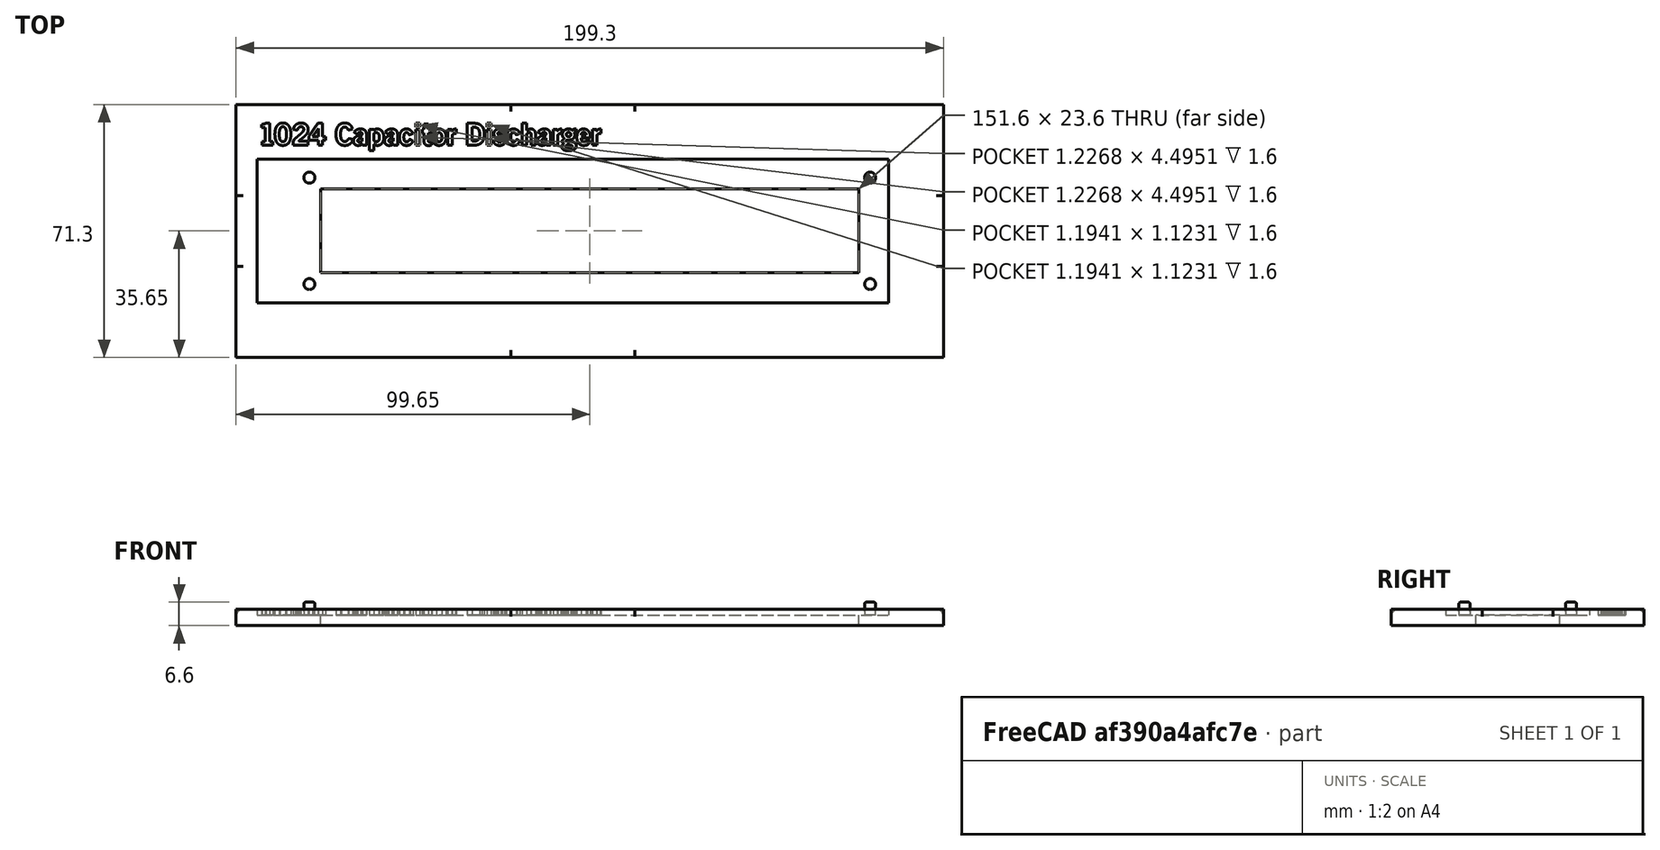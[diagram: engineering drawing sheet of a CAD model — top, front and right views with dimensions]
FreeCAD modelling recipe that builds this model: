
FCSTD DOCUMENT  (FreeCAD 0.21R33771 (Git))
Label: Solder Stencil Jig V2
License: All rights reserved
LicenseURL: http://en.wikipedia.org/wiki/All_rights_reserved
objects: Sketcher::SketchObject×6, PartDesign::Pocket×4, PartDesign::Pad×3, Spreadsheet::Sheet×1, Part::Part2DObjectPython×1, PartDesign::Fillet×1, PartDesign::Body×1, App::Part×1, Mesh::Feature×1
note: 24 computed .brp shape members not serialized (recipe doc carries the construction recipe); baked Part::Feature solids carry a one-line shape summary decoded from their .brp

FEATURE [Spreadsheet::Sheet] Spreadsheet  label="S"
  cells = A1='1024 Capacitor Discharger; A2='Solder Stencil Jig; A4='Board Edge Dimension X; B4='pcb_x; C4(pcb_x)==177.5 mm; D4='Design X dimension of PCB; A5='Board Edge Dimension Y; B5='pcb_y; C5(pcb_y)==40 mm; D5='Design Y dimension of PCB; A6='Board Thickness Z; B6='pcb_z; C6(pcb_z)==1.6 mm; D6='Design Z (thickness) dimension of PCB; A7='Mounting Hole 1 X Coordinate; B7='h1_x; C7(h1_x)==14.5 mm; D7='Relative to lower left corner of PCB, positive X to right, positive Y to top, note the Y coordinate sign is opposite KiCAD; A8='Mounting Hole 1 Y Coordinate; B8='h1_y; C8(h1_y)==5 mm; D8='Mounting Hole 1 = Lower Left, will be one of the registration pins; A9='Mounting Hole 1 Diameter; B9='h1_d; C9(h1_d)==3.2 mm; A10='Mounting Hole 2 X Coordinate; B10='h2_x; C10(h2_x)==14.5 mm; D10='Mounting Hole 2 = Upper Left, no registration; A11='Mounting Hole 2 Y Coordinate; B11='h2_y; C11(h2_y)==35 mm; A12='Mounting Hole 2 Diameter; B12='h2_d; C12(h2_d)==3.2 mm; A13='Mounting Hole 3 X Coordinate; B13='h3_x; C13(h3_x)==172.5 mm; D13='Mounting Hole 3 = Upper Right, will be one of the registration pins; A14='Mounting Hole 3 Y Coordinate; B14='h3_y; C14(h3_y)==35 mm; A15='Mounting Hole 3 Diameter; B15='h3_d; C15(h3_d)==3.2 mm; A16='Mounting Hole 4 X Coordinate; B16='h4_x; C16(h4_x)==172.5 mm; D16='Mounting Hole 4 = Lower Right, no registration; A17='Mounting Hole 4 Y Coordinate; B17='h4_y; C17(h4_y)==5 mm; A18='Mounting Hole 4 Diameter; B18='h4_d; C18(h4_d)==3.2 mm; A19='Holding Ledge Top; B19='hold_t; C19(hold_t)==8.2 mm; D19='The distance of the edge of the printed jig that will hold the PCB from the bottom, make sure this clears any bottom-mounted components; A20='Holding Ledge Bottom; B20='hold_b; C20(hold_b)==8.2 mm; D20='But, the ledges must encompass all mounting holes; A21='Holding Ledge Left; B21='hold_l; C21(hold_l)==17.7 mm; A22='Holding Ledge Right; B22='hold_r; C22(hold_r)==8.2 mm; A23='Bottom PCB Component Clearance; B23='hold_h; C23(hold_h)==3 mm; D23='The window underneath the PCB will be this far off the bottom surface to allow bottom-mounted components clearance; A24='Board-Jig Edge Clearance; B24='edge_clr; C24(edge_clr)==0.25 mm; D24='The window where the PCB sits will be backset from the board edge by this amount on each edge; A25='Mounting Hole Clearance; B25='mh_clr; C25(mh_clr)==0.1 mm; D25='The jig pins and registration pins that go through the mounting holes will clear the PCB by this amount; A26='Registration Pin Height; B26='reg_h; C26(reg_h)==2 mm; D26='The registration pins will be above the PCB surface by this amount to hold the stencil; A27='Jig Oversize Left; B27='jigovr_l; C27(jigovr_l)==6.15 mm; D27='The jig will be this much larger than the PCB in the X direction on the left side, make this at least as large as your stencil; A28='Jig Oversize Right; B28='jigovr_r; C28(jigovr_r)==15.65 mm; D28='The jig will be this much larger than the PCB in the X direction on the right side, make this at least as large as your stencil; A29='Jig Oversize Top; B29='jigove_t; C29(jigove_t)==15.65 mm; D29='The jig will be this much larger than the PCB in the Y direction on the top side, make this at least as large as your stencil; A30='Jig Oversize Bottom; B30='jigovr_b; C30(jigovr_b)==15.65 mm; D30='The jig will be this much larger than the PCB in the Y direction on the bottom side, make this at least as large as your stencil; A31='Jig Top Text; B31='text; C31(text)='1024 Capacitor Discharger; D31='This text will be embossed on the top of the jig; A32='Jig Edge Relief Round Diameter; B32='relf_r; C32(relf_r)==2 mm; D32='The reliefs on the edge of the jig will be rounded to this radius; A33='Jig Edge Relief Size T-B; B33='relf_stb; C33(relf_stb)==35 mm; D33='The reliefs on the top/bottom edge of the jig will be this long, centered on each edge; A34='Jig Edge Relief Size L-R; B34='relf_slr; C34(relf_slr)==20 mm; D34='The reliefs on the left/right edge of the jig will be this long, centered on each edge
FEATURE [Sketcher::SketchObject] Sketch  label="Sketch-Bottom"
  FullyConstrained = true
  MapMode = 5
  Support = -> [XY_Plane001]
  expr: Constraints[10] = <<S>>.pcb_y - <<S>>.hold_b - <<S>>.hold_t
  expr: Constraints[11] = <<S>>.pcb_x - <<S>>.hold_l - <<S>>.hold_r
  expr: Constraints[20] = <<S>>.jigovr_l
  expr: Constraints[21] = <<S>>.jigovr_b
  expr: Constraints[22] = <<S>>.pcb_x + <<S>>.jigovr_l + <<S>>.jigovr_r
  expr: Constraints[23] = <<S>>.pcb_y + <<S>>.jigovr_b + <<S>>.jigove_t
  expr: Constraints[8] = <<S>>.hold_l
  expr: Constraints[9] = <<S>>.hold_b
  sketch-geometry (8):
    g0: LineSegment StartX=17.7 StartY=8.2 StartZ=0 EndX=169.3 EndY=8.2 EndZ=0
    g1: LineSegment StartX=169.3 StartY=8.2 StartZ=0 EndX=169.3 EndY=31.8 EndZ=0
    g2: LineSegment StartX=169.3 StartY=31.8 StartZ=0 EndX=17.7 EndY=31.8 EndZ=0
    g3: LineSegment StartX=17.7 StartY=31.8 StartZ=0 EndX=17.7 EndY=8.2 EndZ=0
    g4: LineSegment StartX=-6.15 StartY=55.65 StartZ=0 EndX=193.15 EndY=55.65 EndZ=0
    g5: LineSegment StartX=193.15 StartY=55.65 StartZ=0 EndX=193.15 EndY=-15.65 EndZ=0
    g6: LineSegment StartX=193.15 StartY=-15.65 StartZ=0 EndX=-6.15 EndY=-15.65 EndZ=0
    g7: LineSegment StartX=-6.15 StartY=-15.65 StartZ=0 EndX=-6.15 EndY=55.65 EndZ=0
  constraints (24):
    c: Coincident(g0,g1)
    c: Coincident(g1,g2)
    c: Coincident(g2,g3)
    c: Coincident(g3,g0)
    c: Horizontal(g0)
    c: Horizontal(g2)
    c: Vertical(g1)
    c: Vertical(g3)
    c: DistanceX(g-1,g0) = 17.7
    c: DistanceY(g-1,g0) = 8.2
    c: DistanceY(g3,g3) = 23.6
    c: DistanceX(g2,g2) = 151.6
    c: Coincident(g4,g5)
    c: Coincident(g5,g6)
    c: Coincident(g6,g7)
    c: Coincident(g7,g4)
    c: Horizontal(g4)
    c: Horizontal(g6)
    c: Vertical(g5)
    c: Vertical(g7)
    c: DistanceX(g6,g-1) = 6.15
    c: DistanceY(g6,g-1) = 15.65
    c: DistanceX(g6,g6) = 199.3
    c: DistanceY(g7,g7) = 71.3
FEATURE [PartDesign::Pad] Pad  label="Pad-MainJig"
  Direction = (0,0,1)
  Length = 4.6
  Length2 = 10
  Profile = -> Sketch
  ReferenceAxis = -> Sketch [N_Axis]
  Type = 0
  expr: Length = <<S>>.pcb_z + <<S>>.hold_h
FEATURE [Sketcher::SketchObject] Sketch001  label="Sketch-PCB"
  AttachmentOffset = pos=(0,0,4.6) rot=(0,0,1;0rad)
  FullyConstrained = true
  MapMode = 5
  Placement = pos=(0,0,4.6) rot=(0,0,1;0rad)
  Support = -> [XY_Plane001]
  expr: .AttachmentOffset.Base.z = <<S>>.pcb_z + <<S>>.hold_h
  expr: Constraints[10] = <<S>>.pcb_y + 2 * <<S>>.edge_clr
  expr: Constraints[11] = <<S>>.pcb_x + 2 * <<S>>.edge_clr
  expr: Constraints[8] = <<S>>.edge_clr
  expr: Constraints[9] = <<S>>.edge_clr
  sketch-geometry (4):
    g0: LineSegment StartX=-0.25 StartY=40.25 StartZ=0 EndX=177.75 EndY=40.25 EndZ=0
    g1: LineSegment StartX=177.75 StartY=40.25 StartZ=0 EndX=177.75 EndY=-0.25 EndZ=0
    g2: LineSegment StartX=177.75 StartY=-0.25 StartZ=0 EndX=-0.25 EndY=-0.25 EndZ=0
    g3: LineSegment StartX=-0.25 StartY=-0.25 StartZ=0 EndX=-0.25 EndY=40.25 EndZ=0
  constraints (12):
    c: Coincident(g0,g1)
    c: Coincident(g1,g2)
    c: Coincident(g2,g3)
    c: Coincident(g3,g0)
    c: Horizontal(g0)
    c: Horizontal(g2)
    c: Vertical(g1)
    c: Vertical(g3)
    c: DistanceX(g2,g-1) = 0.25
    c: DistanceY(g2,g-1) = 0.25
    c: DistanceY(g3,g3) = 40.5
    c: DistanceX(g0,g0) = 178
FEATURE [PartDesign::Pocket] Pocket  label="Pocket-PCB"
  BaseFeature = -> Pad
  Direction = (0,0,-1)
  Length = 1.6
  Length2 = 5
  Profile = -> Sketch001
  ReferenceAxis = -> Sketch001 [N_Axis]
  Type = 0
  expr: Length = <<S>>.pcb_z
FEATURE [Sketcher::SketchObject] Sketch002  label="Sketch-NonRegMountHoles"
  AttachmentOffset = pos=(0,0,3) rot=(0,0,1;0rad)
  FullyConstrained = true
  MapMode = 5
  Placement = pos=(0,0,3) rot=(0,0,1;0rad)
  Support = -> [XY_Plane001]
  expr: .AttachmentOffset.Base.z = <<S>>.hold_h
  expr: Constraints[0] = <<S>>.h2_x
  expr: Constraints[1] = <<S>>.h2_y
  expr: Constraints[2] = <<S>>.h2_d - <<S>>.mh_clr
  expr: Constraints[3] = <<S>>.h4_x
  expr: Constraints[4] = <<S>>.h4_y
  expr: Constraints[5] = <<S>>.h4_d - <<S>>.mh_clr
  sketch-geometry (2):
    g0: Circle CenterX=14.5 CenterY=35 CenterZ=0 NormalX=0 NormalY=0 NormalZ=1 AngleXU=0 Radius=1.55
    g1: Circle CenterX=172.5 CenterY=5 CenterZ=0 NormalX=0 NormalY=0 NormalZ=1 AngleXU=0 Radius=1.55
  constraints (6):
    c: DistanceX(g-1,g0) = 14.5
    c: DistanceY(g-1,g0) = 35
    c: Diameter(g0) = 3.1
    c: DistanceX(g-1,g1) = 172.5
    c: DistanceY(g-1,g1) = 5
    c: Diameter(g1) = 3.1
FEATURE [PartDesign::Pad] Pad001  label="Pad-NonRegMountHoles"
  BaseFeature = -> Pocket
  Direction = (0,0,1)
  Length = 1.5
  Length2 = 10
  Profile = -> Sketch002
  ReferenceAxis = -> Sketch002 [N_Axis]
  Type = 0
  expr: Length = <<S>>.pcb_z - <<S>>.mh_clr
FEATURE [Sketcher::SketchObject] Sketch003  label="Sketch-RegMountHoles"
  AttachmentOffset = pos=(0,0,3) rot=(0,0,1;0rad)
  FullyConstrained = true
  MapMode = 5
  Placement = pos=(0,0,3) rot=(0,0,1;0rad)
  Support = -> [XY_Plane001]
  expr: .AttachmentOffset.Base.z = <<S>>.hold_h
  expr: Constraints[0] = <<S>>.h1_x
  expr: Constraints[1] = <<S>>.h1_y
  expr: Constraints[2] = <<S>>.h1_d - <<S>>.mh_clr
  expr: Constraints[3] = <<S>>.h3_x
  expr: Constraints[4] = <<S>>.h3_y
  expr: Constraints[5] = <<S>>.h3_d - <<S>>.mh_clr
  sketch-geometry (2):
    g0: Circle CenterX=14.5 CenterY=5 CenterZ=0 NormalX=0 NormalY=0 NormalZ=1 AngleXU=0 Radius=1.55
    g1: Circle CenterX=172.5 CenterY=35 CenterZ=0 NormalX=0 NormalY=0 NormalZ=1 AngleXU=0 Radius=1.55
  constraints (6):
    c: DistanceX(g-1,g0) = 14.5
    c: DistanceY(g-1,g0) = 5
    c: Diameter(g0) = 3.1
    c: DistanceX(g-1,g1) = 172.5
    c: DistanceY(g-1,g1) = 35
    c: Diameter(g1) = 3.1
FEATURE [PartDesign::Pad] Pad002  label="Pad-RegMountHoles"
  BaseFeature = -> Pad001
  Direction = (0,0,1)
  Length = 3.6
  Length2 = 10
  Profile = -> Sketch003
  ReferenceAxis = -> Sketch003 [N_Axis]
  Type = 0
  expr: Length = <<S>>.pcb_z + <<S>>.reg_h
FEATURE [Part::Part2DObjectPython] ShapeString  label="ShapeString-Text"  # Draft 2D object (typed FeaturePython)
  FontFile = <path> Capacitor Discharger/FreeCAD Project/New folder/OldSansBlack.ttf
  MakeFace = true
  Placement = pos=(0,44.25,4.6) rot=(0,0,1;0rad)
  Size = 3.4125
  String = 1024 Capacitor Discharger
  Tracking = 0
  expr: .Placement.Base.y = <<S>>.pcb_y + 4 mm + <<S>>.edge_clr
  expr: .Placement.Base.z = <<S>>.hold_h + <<S>>.pcb_z
  expr: Size = (<<S>>.jigove_t - 2 mm) / 4
  expr: String = <<S>>.text
FEATURE [PartDesign::Pocket] Pocket001  label="Pocket-Test"
  BaseFeature = -> Pad002
  Direction = (0,0,-1)
  Length = 1.6
  Length2 = 5
  Profile = -> ShapeString
  ReferenceAxis = -> ShapeString [N_Axis]
  Type = 0
  expr: Length = <<S>>.pcb_z
FEATURE [Sketcher::SketchObject] Sketch004  label="Sketch-TopBotReliefs"
  AttachmentOffset = pos=(0,0,88.75) rot=(0,0,1;0rad)
  FullyConstrained = true
  MapMode = 5
  Placement = pos=(88.75,-1.97e-14,1.97e-14) rot=(0.57735,0.57735,0.57735;2.0944rad)
  Support = -> [YZ_Plane001]
  expr: .AttachmentOffset.Base.z = <<S>>.pcb_x / 2
  expr: Constraints[12] = <<S>>.pcb_y + <<S>>.jigove_t
  expr: Constraints[13] = <<S>>.hold_h + <<S>>.pcb_z
  expr: Constraints[14] = <<S>>.relf_r
  expr: Constraints[2] = <<S>>.jigovr_b
  expr: Constraints[3] = <<S>>.pcb_z + <<S>>.hold_h
  expr: Constraints[4] = <<S>>.relf_r
  sketch-geometry (6):
    g0: ArcOfCircle CenterX=-13.65 CenterY=2.6 CenterZ=0 NormalX=0 NormalY=0 NormalZ=1 AngleXU=0 Radius=2 StartAngle=1.5708 EndAngle=3.14159
    g1: LineSegment StartX=-13.65 StartY=4.6 StartZ=0 EndX=-15.65 EndY=4.6 EndZ=0
    g2: LineSegment StartX=-15.65 StartY=4.6 StartZ=0 EndX=-15.65 EndY=2.6 EndZ=0
    g3: ArcOfCircle CenterX=53.65 CenterY=2.6 CenterZ=0 NormalX=0 NormalY=0 NormalZ=1 AngleXU=0 Radius=2 StartAngle=1.8311e-12 EndAngle=1.5708
    g4: LineSegment StartX=53.65 StartY=4.6 StartZ=0 EndX=55.65 EndY=4.6 EndZ=0
    g5: LineSegment StartX=55.65 StartY=4.6 StartZ=0 EndX=55.65 EndY=2.6 EndZ=0
  constraints (20):
    c: Vertical(g0,g0)
    c: Angle(g0) = 1.5708
    c: DistanceX(g0,g-1) = 15.65
    c: DistanceY(g-1,g0) = 4.6
    c: Radius(g0) = 2
    c: Coincident(g1,g0)
    c: Horizontal(g1)
    c: Coincident(g2,g1)
    c: Coincident(g2,g0)
    c: Vertical(g2)
    c: Vertical(g3,g3)
    c: Angle(g3) = 1.5708
    c: DistanceX(g-1,g3) = 55.65
    c: DistanceY(g-1,g3) = 4.6
    c: Radius(g3) = 2
    c: Coincident(g4,g3)
    c: Horizontal(g4)
    c: Coincident(g5,g4)
    c: Coincident(g5,g3)
    c: Vertical(g5)
FEATURE [PartDesign::Pocket] Pocket002  label="Pocket-TopBotReliefs"
  BaseFeature = -> Pocket001
  Direction = (-1,2e-16,-3e-16)
  Length = 35
  Length2 = 5
  Midplane = true
  Profile = -> Sketch004
  ReferenceAxis = -> Sketch004 [N_Axis]
  Type = 0
  expr: Length = Spreadsheet.relf_stb
FEATURE [Sketcher::SketchObject] Sketch005  label="Sketch-LeftRightReliefs"
  AttachmentOffset = pos=(0,0,-20) rot=(0,0,1;0rad)
  FullyConstrained = true
  MapMode = 5
  Placement = pos=(0,20,4.4e-15) rot=(1,0,0;1.5708rad)
  Support = -> [XZ_Plane001]
  expr: .AttachmentOffset.Base.z = -<<S>>.pcb_y / 2
  expr: Constraints[12] = <<S>>.pcb_x + <<S>>.jigovr_r
  expr: Constraints[13] = <<S>>.hold_h + <<S>>.pcb_z
  expr: Constraints[14] = <<S>>.relf_r
  expr: Constraints[2] = <<S>>.jigovr_l
  expr: Constraints[3] = <<S>>.hold_h + <<S>>.pcb_z
  expr: Constraints[4] = <<S>>.relf_r
  sketch-geometry (6):
    g0: ArcOfCircle CenterX=-4.15 CenterY=2.6 CenterZ=0 NormalX=0 NormalY=0 NormalZ=1 AngleXU=0 Radius=2 StartAngle=1.5708 EndAngle=3.14159
    g1: LineSegment StartX=-4.15 StartY=4.6 StartZ=0 EndX=-6.15 EndY=4.6 EndZ=0
    g2: LineSegment StartX=-6.15 StartY=2.6 StartZ=0 EndX=-6.15 EndY=4.6 EndZ=0
    g3: ArcOfCircle CenterX=191.15 CenterY=2.6 CenterZ=0 NormalX=0 NormalY=0 NormalZ=1 AngleXU=0 Radius=2 StartAngle=4.794e-13 EndAngle=1.5708
    g4: LineSegment StartX=193.15 StartY=4.6 StartZ=0 EndX=191.15 EndY=4.6 EndZ=0
    g5: LineSegment StartX=193.15 StartY=4.6 StartZ=0 EndX=193.15 EndY=2.6 EndZ=0
  constraints (20):
    c: Vertical(g0,g0)
    c: Angle(g0) = 1.5708
    c: DistanceX(g0,g-1) = 6.15
    c: DistanceY(g-1,g0) = 4.6
    c: Radius(g0) = 2
    c: Coincident(g1,g0)
    c: Horizontal(g1)
    c: Coincident(g2,g0)
    c: Coincident(g2,g1)
    c: Vertical(g2)
    c: Vertical(g3,g3)
    c: Angle(g3) = 1.5708
    c: DistanceX(g-1,g3) = 193.15
    c: DistanceY(g-1,g3) = 4.6
    c: Radius(g3) = 2
    c: Coincident(g4,g3)
    c: Horizontal(g4)
    c: Coincident(g5,g4)
    c: Coincident(g5,g3)
    c: Vertical(g5)
FEATURE [PartDesign::Pocket] Pocket003  label="Pocket-LeftRightReliefs"
  BaseFeature = -> Pocket002
  Direction = (0,1,2e-16)
  Length = 20
  Length2 = 5
  Midplane = true
  Profile = -> Sketch005
  ReferenceAxis = -> Sketch005 [N_Axis]
  Type = 0
  expr: Length = <<S>>.relf_slr
FEATURE [PartDesign::Fillet] Fillet  label="Fillet-RegistrationPins"
  Base = -> Pocket003 [Edge1527,Edge1531,Edge1533,Edge1529]
  BaseFeature = -> Pocket003
  Radius = 0.5
  SupportTransform = false
  UseAllEdges = false
FEATURE [PartDesign::Body] Body  label="Body-SolderStencilJig"
  Group = -> [Sketch,Pad,Sketch001,Pocket,Sketch002,Pad001,Sketch003,Pad002,ShapeString,Pocket001,Sketch004,Pocket002,Sketch005,Pocket003,Fillet]
  Origin = -> Origin001
  Tip = -> Fillet
FEATURE [App::Part] Part  label="Part-SolderStencilJig"
  Group = -> [Body]
  Origin = -> Origin
FEATURE [Mesh::Feature] Mesh  label="Body-SolderStencilJig (Meshed)"
note: 1 file-system path scrubbed to <path> (originals preserved in the JSON sidecar)
